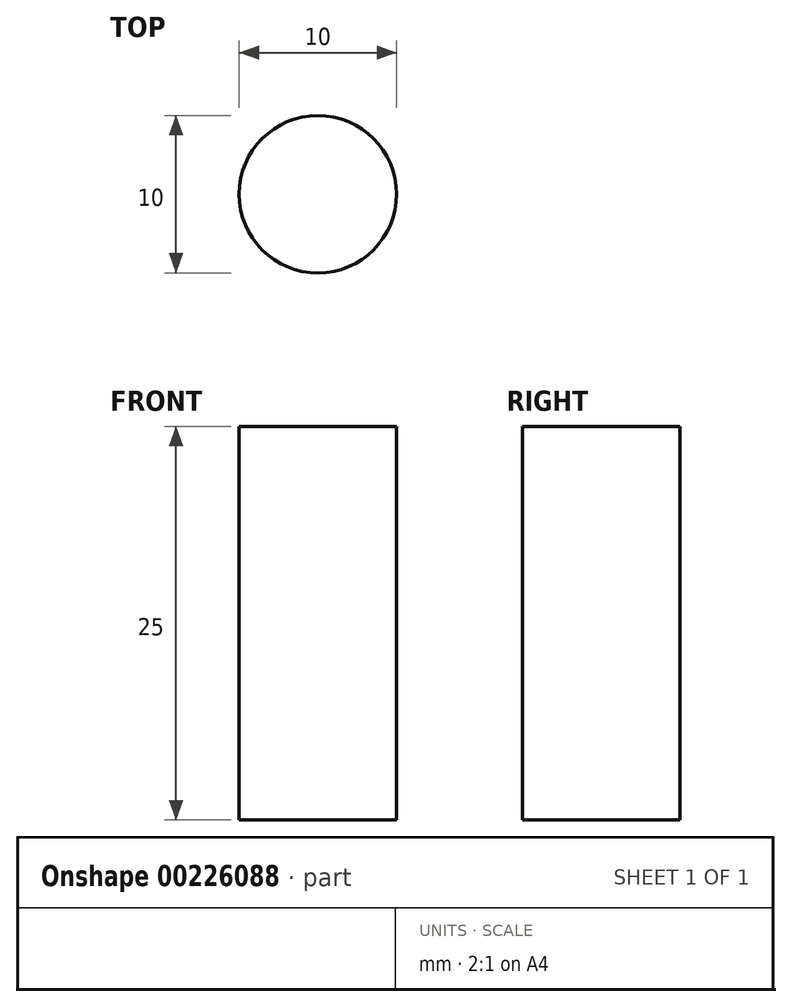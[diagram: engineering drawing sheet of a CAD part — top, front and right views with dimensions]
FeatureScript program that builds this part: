
annotation { "Feature Type Name" : "Feature", "Feature Type Description" : "" }
export const myFeature = defineFeature(function(context is Context, id is Id, definition is map)
    precondition{}
    {
        {
            var Q0;
            Q0=qCreatedBy(makeId("Top.planeOp"),FACE);
            var sketch = newSketch(context, id + "F0", { "sketchPlane" : qUnion([Q0])});
            skCircle(sketch, "E0", {"center": v(0, 0) * mm, "radius": 3 * mm});
            skCircle(sketch, "E1", {"center": v(0, 0) * mm, "radius": 5 * mm});
            skSolve(sketch);
        }
        {
            var Q0;
            Q0=sQuery(id+"F0.wireOp",EDGE,"E1");
            extrude(context, id + "F1", {"bodyType" : ToolBodyType.SURFACE, "surfaceEntities" : qUnion([Q0]), "depth" : 25 * mm});
        }
    });
